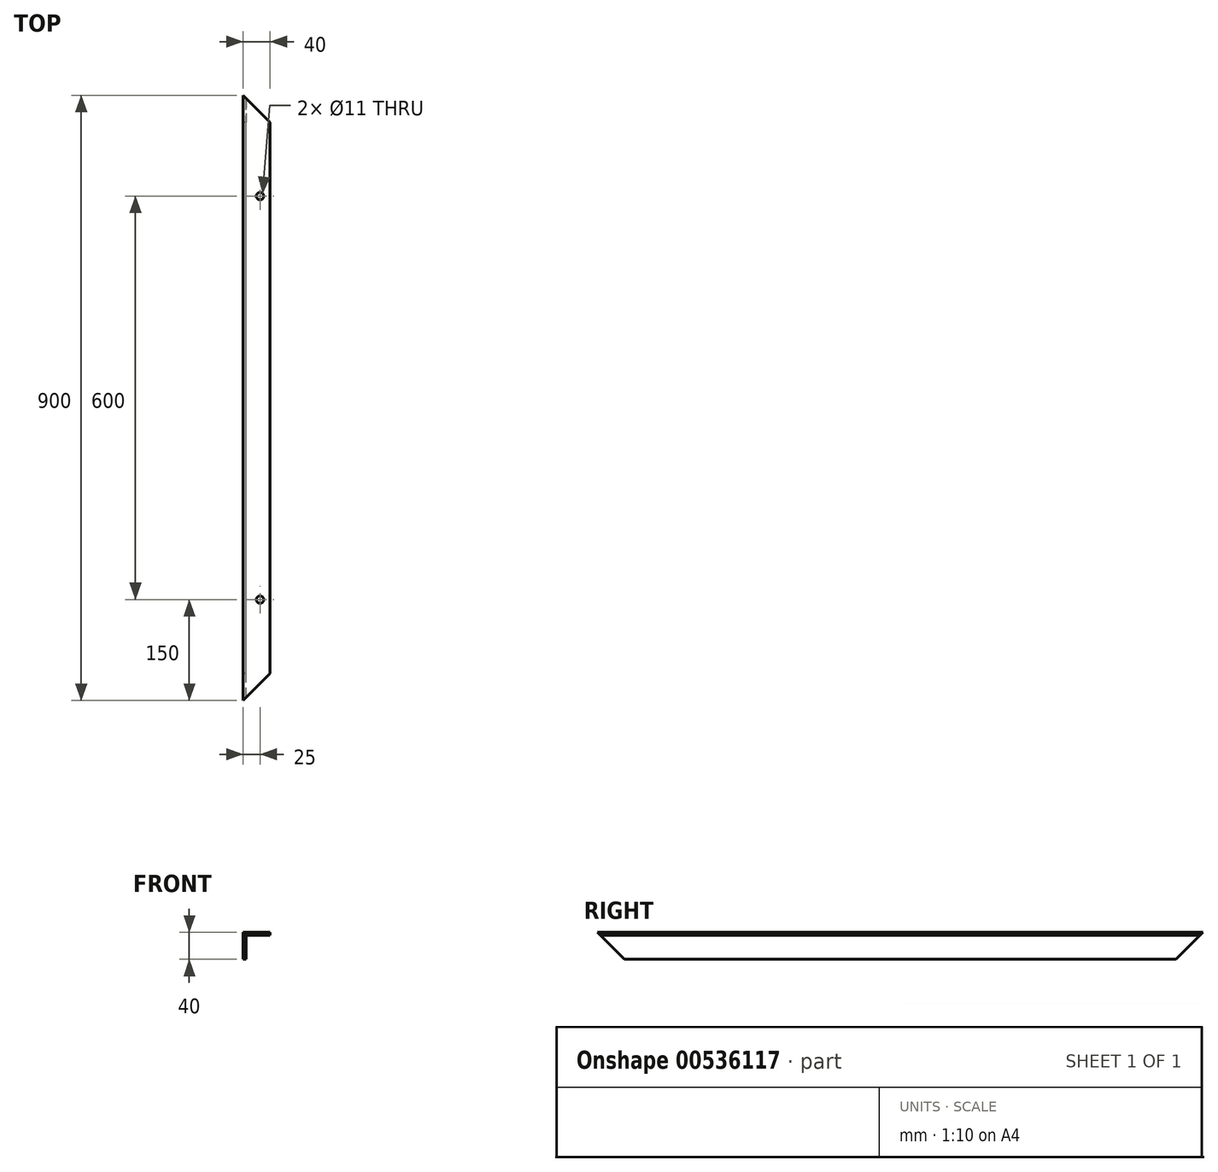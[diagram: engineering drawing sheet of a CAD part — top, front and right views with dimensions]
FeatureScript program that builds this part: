
annotation { "Feature Type Name" : "Feature", "Feature Type Description" : "" }
export const myFeature = defineFeature(function(context is Context, id is Id, definition is map)
    precondition{}
    {
        {
            var Q0;
            Q0=qCreatedBy(makeId("Front.planeOp"),FACE);
            var sketch = newSketch(context, id + "F0", { "sketchPlane" : qUnion([Q0])});
            skLineSegment(sketch, "E0", {"start": v(0, 0) * mm, "end": v(0, 40) * mm});
            skLineSegment(sketch, "E1", {"start": v(0, 40) * mm, "end": v(40, 40) * mm});
            skLineSegment(sketch, "E2.0", {"start": v(4, 36) * mm, "end": v(40, 36) * mm});
            skLineSegment(sketch, "E2.1", {"start": v(4, 0) * mm, "end": v(4, 36) * mm});
            skLineSegment(sketch, "E3", {"start": v(0, 0) * mm, "end": v(4, 0) * mm});
            skLineSegment(sketch, "E4", {"start": v(40, 36) * mm, "end": v(40, 40) * mm});
            skSolve(sketch);
        }
        {
            var Q0;
            Q0=makeQuery(id+"F0.imprint","IMPRINT",FACE,{"disambiguationData":[TD([[makeQuery(id+"F0.imprint","IMPRINT",EDGE,{"derivedFrom":sQuery(id+"F0.wireOp",EDGE,"E0")}),-1.0]])]});
            extrude(context, id + "F1", {"entities" : qUnion([Q0]), "endBound" : BoundingType.SYMMETRIC, "depth" : 900 * mm, "offsetDistance" : 25 * mm});
        }
        {
            var Q0;
            Q0=makeQuery(id+"F1.opExtrude","SWEPT_FACE",FACE,{"disambiguationData":[OSD([sQuery(id+"F0.wireOp",EDGE,"E0")])]});
            var sketch = newSketch(context, id + "F2", { "sketchPlane" : qUnion([Q0])});
            skLineSegment(sketch, "E5", {"start": v(-450, 40) * mm, "end": v(-410, 0) * mm});
            skLineSegment(sketch, "E6", {"start": v(450, 40) * mm, "end": v(410, 0) * mm});
            skSolve(sketch);
        }
        {
            var Q0;
            {var subQ0=sQuery(id+"F2.wireOp",EDGE,"E5");Q0=makeQuery(id+"F2.imprint","IMPRINT",FACE,{"disambiguationData":[TD([[makeQuery(id+"F2.imprint","IMPRINT",EDGE,{"derivedFrom":subQ0}),-1.0]])]});}
            var Q1;
            {var subQ0=sQuery(id+"F2.wireOp",EDGE,"E6");Q1=makeQuery(id+"F2.imprint","IMPRINT",FACE,{"disambiguationData":[TD([[makeQuery(id+"F2.imprint","IMPRINT",EDGE,{"derivedFrom":subQ0}),1.0]])]});}
            extrude(context, id + "F3", {"entities" : qUnion([Q0, Q1]), "operationType" : NewBodyOperationType.REMOVE, "oppositeDirection" : true, "depth" : 40 * mm, "offsetDistance" : 25 * mm});
        }
        {
            var Q0;
            Q0=makeQuery(id+"F1.opExtrude","SWEPT_FACE",FACE,{"disambiguationData":[OSD([sQuery(id+"F0.wireOp",EDGE,"E1")])]});
            var sketch = newSketch(context, id + "F4", { "sketchPlane" : qUnion([Q0])});
            skLineSegment(sketch, "E7", {"start": v(0, 450) * mm, "end": v(40, 410) * mm});
            skLineSegment(sketch, "E8", {"start": v(0, -450) * mm, "end": v(40, -410) * mm});
            skSolve(sketch);
        }
        {
            var Q0;
            {var subQ0=sQuery(id+"F4.wireOp",EDGE,"E7");Q0=makeQuery(id+"F4.imprint","IMPRINT",FACE,{"disambiguationData":[TD([[makeQuery(id+"F4.imprint","IMPRINT",EDGE,{"derivedFrom":subQ0}),1.0]])]});}
            var Q1;
            {var subQ0=sQuery(id+"F4.wireOp",EDGE,"E8");Q1=makeQuery(id+"F4.imprint","IMPRINT",FACE,{"disambiguationData":[TD([[makeQuery(id+"F4.imprint","IMPRINT",EDGE,{"derivedFrom":subQ0}),-1.0]])]});}
            extrude(context, id + "F5", {"entities" : qUnion([Q0, Q1]), "operationType" : NewBodyOperationType.REMOVE, "oppositeDirection" : true, "depth" : 40 * mm, "offsetDistance" : 25 * mm});
        }
        {
            var Q0;
            Q0=makeQuery(id+"F1.opExtrude","SWEPT_FACE",FACE,{"disambiguationData":[OSD([sQuery(id+"F0.wireOp",EDGE,"E1")])]});
            var sketch = newSketch(context, id + "F6", { "sketchPlane" : qUnion([Q0])});
            skLineSegment(sketch, "E9", {"start": v(0, 450) * mm, "end": v(0, 300) * mm});
            skLineSegment(sketch, "E10", {"start": v(0, 300) * mm, "end": v(25, 300) * mm});
            skLineSegment(sketch, "E11", {"start": v(0, -450) * mm, "end": v(0, -300) * mm});
            skLineSegment(sketch, "E12", {"start": v(0, -300) * mm, "end": v(25, -300) * mm});
            skCircle(sketch, "E13", {"center": v(25, 300) * mm, "radius": 7.46 * mm});
            skCircle(sketch, "E14", {"center": v(25, -300) * mm, "radius": 9.87 * mm});
            skSolve(sketch);
        }
        {
            var Q0;
            Q0=sQuery(id+"F6.wireOp",VERTEX,"E12.end");
            var Q1;
            Q1=sQuery(id+"F6.wireOp",VERTEX,"E10.end");
            var Q2;
            Q2=makeQuery(id+"F1.opExtrude","SWEPT_BODY",BODY,{"disambiguationData":[OSD([sQuery(id+"F0.wireOp",EDGE,"E0"),sQuery(id+"F0.wireOp",EDGE,"E1"),sQuery(id+"F0.wireOp",EDGE,"E2.0"),sQuery(id+"F0.wireOp",EDGE,"E2.1"),sQuery(id+"F0.wireOp",EDGE,"E3"),sQuery(id+"F0.wireOp",EDGE,"E4")])]});
            hole(context, id + "F7", {"style" : HoleStyle.SIMPLE, "endStyle" : HoleEndStyle.THROUGH, "standardTappedOrClearance" : lookupTablePath({ "standard" : "ISO", "fit" : "Normal", "size" : "M10", "type" : "Clearance" }), "standardBlindInLast" : lookupTablePath({ "fit" : "Standard", "standard" : "ISO", "size" : "M10", "type" : "Clearance" }), "holeDiameter" : 11 * mm, "isTappedThrough" : true, "tappedDepth" : 12 * mm, "tapClearance" : 3, "locations" : qUnion([Q0, Q1]), "scope" : qUnion([Q2])});
        }
    });
